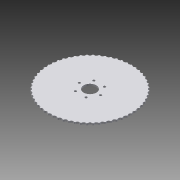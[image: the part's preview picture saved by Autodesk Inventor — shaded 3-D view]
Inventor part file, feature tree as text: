
AUTODESK INVENTOR PART (.ipt)
format: ipt  version: 2015 (Build 190159000, 159)  size: 276,480 bytes
history: native  units: in
note: dims shown in document units (in); Inventor stores cm internally (conversion verified against a paired STEP export)
features: extrude x3, sketch x2, pattern_circular x1, projected_geometry x1
ambient origin geometry x8: Origin, YZ Plane, XZ Plane, XY Plane, X Axis, Y Axis, Z Axis, Center Point
bodies: Solid1 (feature_tree)
feature tree (7):
  sketch  "Sketch1"  dims[d0=7.4in d1=7.2in]
  extrude  "Extrusion1"  Depth=7.2in
  extrude  "Extrusion3"  Depth=0.1619in
  pattern_circular  "Circular Pattern4"  [2 undecoded]
  extrude  "Extrusion4"  Depth=0.1619in TaperAngle=360.0deg
  sketch  "Sketch2"  dims[d2=1.1245in d3=1.875in d4=0.206in d5=2.3622in d7=360.0deg d9=10.2362in d11=360.0deg d13=0.156in d14=0.0in d28=23.622in d30=360.0deg d32=7.2in d33=0.15in d35=0.075in d36=0.075in d37=0.1619in d44=1.0in d45=0.0in d46=23.622in d47=360.0deg d49=1.0in d50=0.0in]
  projected_geometry  "Projected Loop1"
note: 2 required parameter values undecoded (feature->parameter linkage not recoverable at this tier; creation-order binding heuristic only, values carry confidence <= 0.55)
